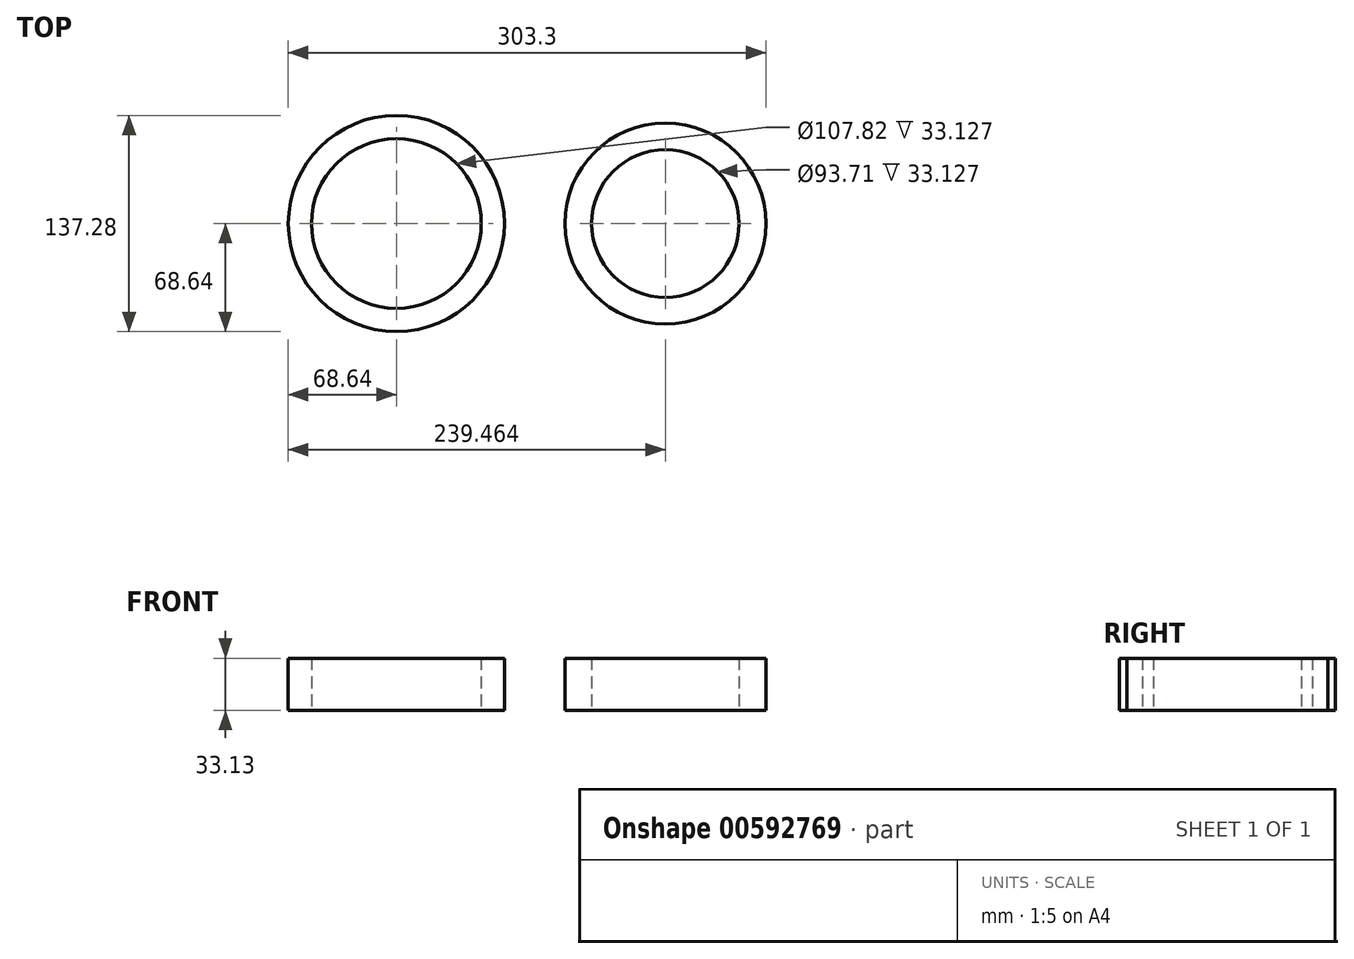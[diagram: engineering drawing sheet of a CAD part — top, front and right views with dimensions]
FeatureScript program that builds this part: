
annotation { "Feature Type Name" : "Feature", "Feature Type Description" : "" }
export const myFeature = defineFeature(function(context is Context, id is Id, definition is map)
    precondition{}
    {
        {
            var Q0;
            Q0=qCreatedBy(makeId("Top.planeOp"),FACE);
            var sketch = newSketch(context, id + "F0", { "sketchPlane" : qUnion([Q0])});
            skCircle(sketch, "E0", {"center": v(0, 0) * mm, "radius": 53.9 * mm});
            skCircle(sketch, "E1", {"center": v(0, 0) * mm, "radius": 68.64 * mm});
            skCircle(sketch, "E2", {"center": v(170.82, 0) * mm, "radius": 46.85 * mm});
            skCircle(sketch, "E3", {"center": v(170.82, 0) * mm, "radius": 63.83 * mm});
            skSolve(sketch);
        }
        {
            var Q0;
            Q0=makeQuery(id+"F0.imprint","IMPRINT",FACE,{"disambiguationData":[TD([[makeQuery(id+"F0.imprint","IMPRINT",EDGE,{"derivedFrom":sQuery(id+"F0.wireOp",EDGE,"E0")}),-1.0]])]});
            var Q1;
            Q1 = qSketchRegion(id + "F0", true);
            extrude(context, id + "F1", {"entities" : qUnion([Q0, Q1]), "depth" : 33.13 * mm, "offsetDistance" : 25.4 * mm});
        }
    });
